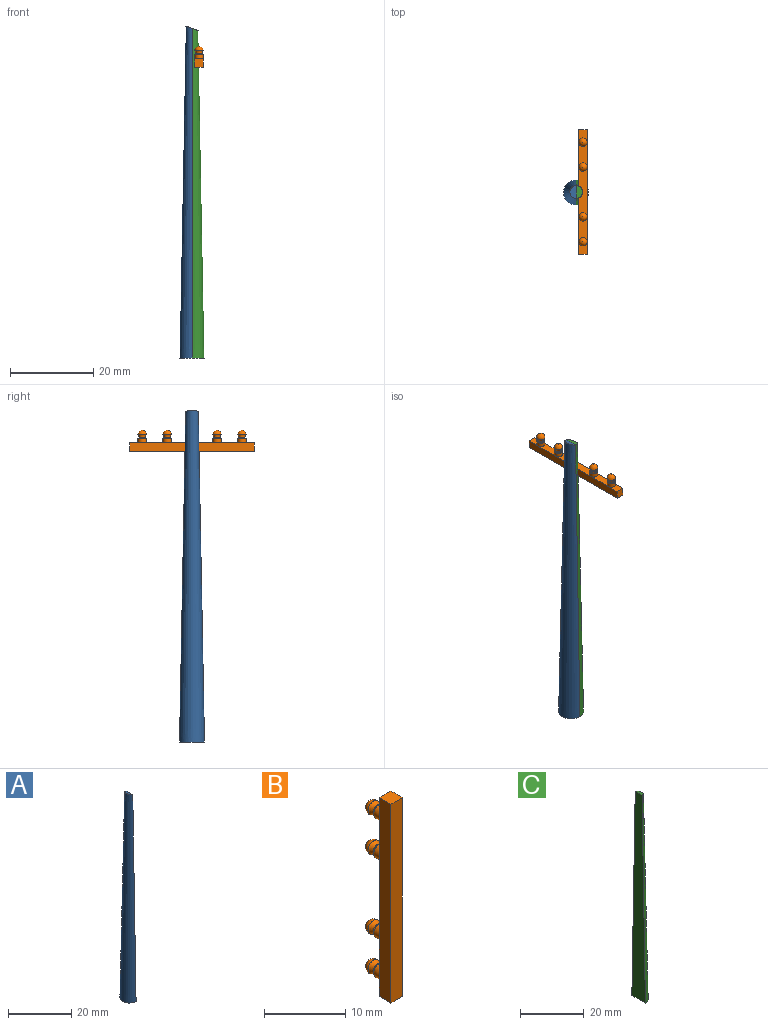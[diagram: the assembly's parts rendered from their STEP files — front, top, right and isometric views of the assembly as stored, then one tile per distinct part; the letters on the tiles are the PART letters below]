
ASSEMBLY  parts=3 mates=2
PART A: 4 faces, bbox 3x6x79.9 mm
  f0: plane 79.36x6mm, normal (1,0,0), area 358.1mm2, adj f1,f2,f3
  f1: plane 3.02x1.5mm, normal (0.35,0,0.94), area 3.8mm2, adj f0,f3
  f2: plane 6x3mm, normal (0,0,-1), area 14.1mm2, adj f0,f3
  f3: cone r=1.5mm half-angle=1.1deg, axis (0,0,-1), area 564.2mm2, adj f0,f1,f2
PART B: 30 faces, bbox 2.3x5x30 mm
  f0: cylinder r=0.75mm len=1.5mm, axis (0,-1,0), area 1.6mm2, adj f21,f23
  f1: cylinder r=0.75mm len=1.5mm, axis (0,-1,0), area 1.6mm2, adj f19,f25
  f2: cylinder r=0.75mm len=1.5mm, axis (0,-1,0), area 1.6mm2, adj f17,f27
  f3: cylinder r=0.75mm len=1.5mm, axis (0,-1,0), area 1.6mm2, adj f15,f29
  f4: plane 6x2mm, normal (0,1,0), area 8.9mm2, adj f9,f11,f18,f20
  f5: plane 3x2mm, normal (0,1,0), area 4.4mm2, adj f9,f11,f13,f18
  f6: plane 12x2mm, normal (0,1,0), area 20.9mm2, adj f9,f11,f16,f20
  f7: plane 6x2mm, normal (0,1,0), area 8.9mm2, adj f9,f11,f14,f16
  f8: plane 3x2mm, normal (0,1,0), area 4.4mm2, adj f9,f11,f12,f14
  f9: plane 30x2mm, normal (-1,0,0), area 60mm2, adj f4,f5,f6,f7,f8,f10,f12,f13
  f10: plane 30x2mm, normal (0,-1,0), area 60mm2, adj f9,f11,f12,f13
  f11: plane 30x2mm, normal (1,0,0), area 60mm2, adj f4,f5,f6,f7,f8,f10,f12,f13
  f12: plane 2x2mm, normal (0,0,1), area 4mm2, adj f8,f9,f10,f11
  f13: plane 2x2mm, normal (0,0,-1), area 4mm2, adj f5,f9,f10,f11
  f14: cylinder r=1mm len=2mm, axis (0,-1,0), area 6.3mm2, adj f7,f8,f15
  f15: plane 2x2mm, normal (0,1,0), area 1.4mm2, adj f3,f14
  f16: cylinder r=1mm len=2mm, axis (0,-1,0), area 6.3mm2, adj f6,f7,f17
  f17: plane 2x2mm, normal (0,1,0), area 1.4mm2, adj f2,f16
  f18: cylinder r=1mm len=2mm, axis (0,-1,0), area 6.3mm2, adj f4,f5,f19
  f19: plane 2x2mm, normal (0,1,0), area 1.4mm2, adj f1,f18
  f20: cylinder r=1mm len=2mm, axis (0,-1,0), area 6.3mm2, adj f4,f6,f21
  f21: plane 2x2mm, normal (0,1,0), area 1.4mm2, adj f0,f20
  f22: sphere r=1mm, area 6.3mm2, adj f23
  f23: torus R=1.75mm, axis (0,1,0), area 3.8mm2, adj f0,f22
  f24: sphere r=1mm, area 6.3mm2, adj f25
  f25: torus R=1.75mm, axis (0,1,0), area 3.8mm2, adj f1,f24
  f26: sphere r=1mm, area 6.3mm2, adj f27
  f27: torus R=1.75mm, axis (0,1,0), area 3.8mm2, adj f2,f26
  f28: sphere r=1mm, area 6.3mm2, adj f29
  f29: torus R=1.75mm, axis (0,1,0), area 3.8mm2, adj f3,f28
PART C: 7 faces, bbox 3x6x79.4 mm
  f0: cone r=1.5mm half-angle=1.1deg, axis (0,0,-1), area 553.1mm2, adj f1,f2,f3,f4,f5,f6
  f1: plane 6x3mm, normal (0,0,-1), area 14.1mm2, adj f0,f6
  f2: plane 3.1x2mm, normal (1,0,0), area 6.1mm2, adj f0,f3,f4
  f3: plane 3.1x1.02mm, normal (0,0,1), area 2.3mm2, adj f0,f2
  f4: plane 3.02x0.98mm, normal (0,0,-1), area 2.1mm2, adj f0,f2
  f5: plane 3.02x1.52mm, normal (0.35,0,0.94), area 3.9mm2, adj f0,f6
  f6: plane 79.36x6mm, normal (-1,0,0), area 358.1mm2, adj f0,f1,f5
PLACE A t=(-53.28,-15.6,-9.76)mm
PLACE B rot(axis=(0,0.71,0.71),180deg) t=(-50.61,-30.6,62.24)mm
PLACE C t=(-53.28,-15.6,-9.76)mm
MATE fastened A.f0 <-> C.f6  axis (1,0,0) through (-53.28,-15.6,-9.76)mm
MATE fastened B.f11 <-> C.f2  axis (-1,0,0) through (-52.61,-15.6,60.24)mm
